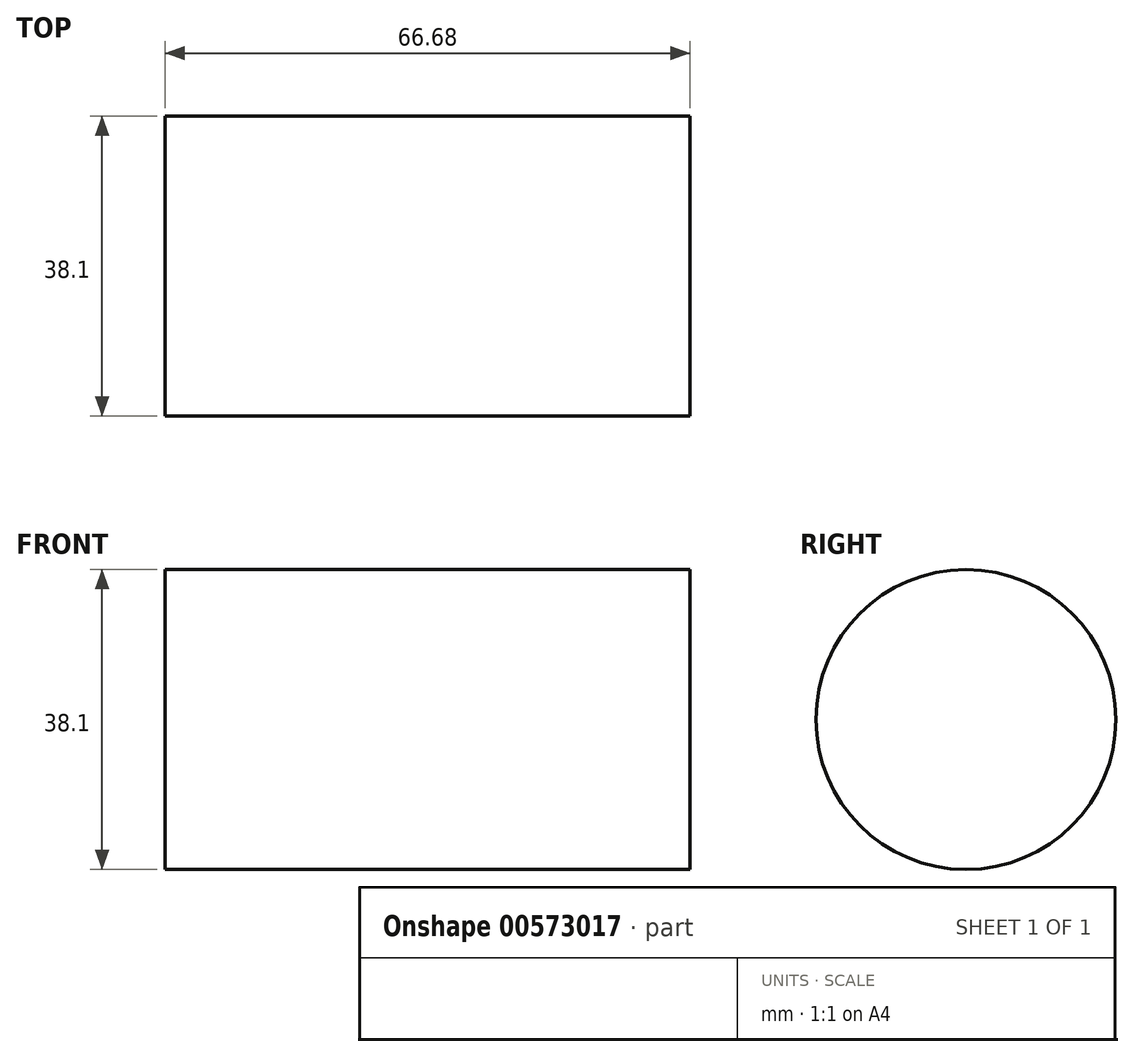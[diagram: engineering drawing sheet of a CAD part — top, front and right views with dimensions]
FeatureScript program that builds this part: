
annotation { "Feature Type Name" : "Feature", "Feature Type Description" : "" }
export const myFeature = defineFeature(function(context is Context, id is Id, definition is map)
    precondition{}
    {
        {
            var Q0;
            Q0=qCreatedBy(makeId("Right.planeOp"),FACE);
            var sketch = newSketch(context, id + "F0", { "sketchPlane" : qUnion([Q0])});
            skCircle(sketch, "E0", {"center": v(0, 0) * mm, "radius": 19.05 * mm});
            skSolve(sketch);
        }
        {
            var Q0;
            Q0=makeQuery(id+"F0.imprint","IMPRINT",FACE,{"disambiguationData":[TD([[makeQuery(id+"F0.imprint","IMPRINT",EDGE,{"derivedFrom":sQuery(id+"F0.wireOp",EDGE,"E0")}),1.0]])]});
            extrude(context, id + "F1", {"entities" : qUnion([Q0]), "endBound" : BoundingType.SYMMETRIC, "depth" : 66.67 * mm, "offsetDistance" : 25.4 * mm});
        }
    });
